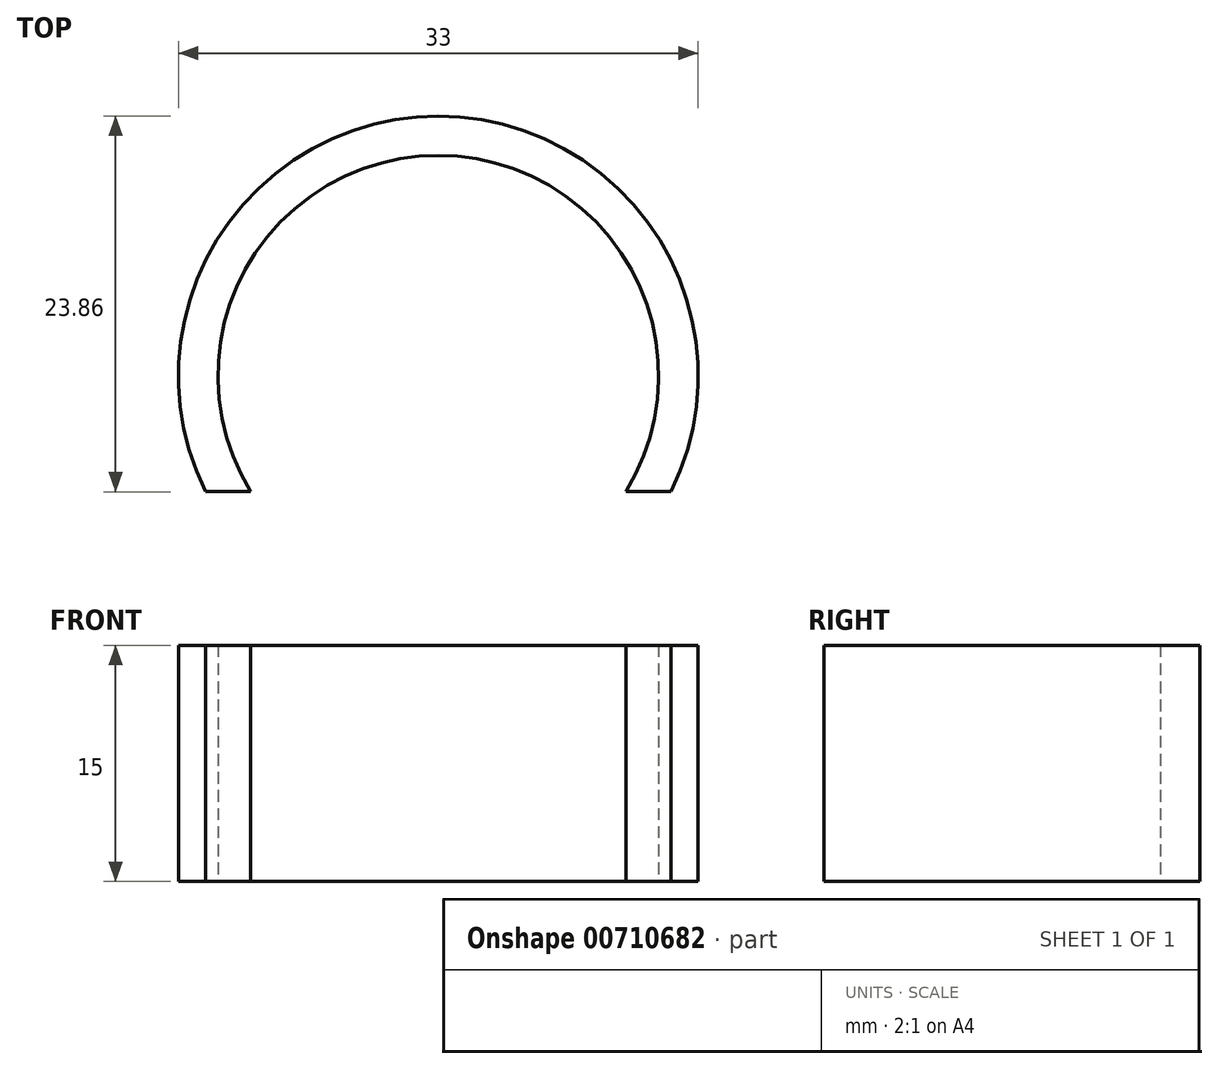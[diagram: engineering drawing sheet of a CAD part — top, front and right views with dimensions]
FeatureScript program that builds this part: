
annotation { "Feature Type Name" : "Feature", "Feature Type Description" : "" }
export const myFeature = defineFeature(function(context is Context, id is Id, definition is map)
    precondition{}
    {
        {
            var Q0;
            Q0=qCreatedBy(makeId("Top.planeOp"),FACE);
            var sketch = newSketch(context, id + "F0", { "sketchPlane" : qUnion([Q0])});
            skArc(sketch, "E0", {"start": v(13.42, -4) * mm, "mid": v(0, 14) * mm, "end": v(-13.42, -4) * mm});
            skArc(sketch, "E1", {"start": v(16, -4) * mm, "mid": v(0, 16.5) * mm, "end": v(-16, -4) * mm});
            skArc(sketch, "E2", {"start": v(-16, -4) * mm, "mid": v(-15.48, -5.71) * mm, "end": v(-14.77, -7.36) * mm});
            skArc(sketch, "E3", {"start": v(-13.42, -4) * mm, "mid": v(-12.77, -5.73) * mm, "end": v(-11.91, -7.36) * mm});
            skLineSegment(sketch, "E4", {"start": v(-14.77, -7.36) * mm, "end": v(-11.91, -7.36) * mm});
            skLineSegment(sketch, "E5.trimOffspring", {"start": v(11.91, -7.36) * mm, "end": v(14.77, -7.36) * mm});
            skArc(sketch, "E6.trimOffspring", {"start": v(14.77, -7.36) * mm, "mid": v(15.48, -5.71) * mm, "end": v(16, -4) * mm});
            skArc(sketch, "E7.trimOffspring", {"start": v(11.91, -7.36) * mm, "mid": v(12.77, -5.73) * mm, "end": v(13.42, -4) * mm});
            skSolve(sketch);
        }
        {
            var Q0;
            Q0 = qSketchRegion(id + "F0", true);
            extrude(context, id + "F1", {"entities" : qUnion([Q0]), "depth" : 15 * mm, "offsetDistance" : 25 * mm});
        }
    });
